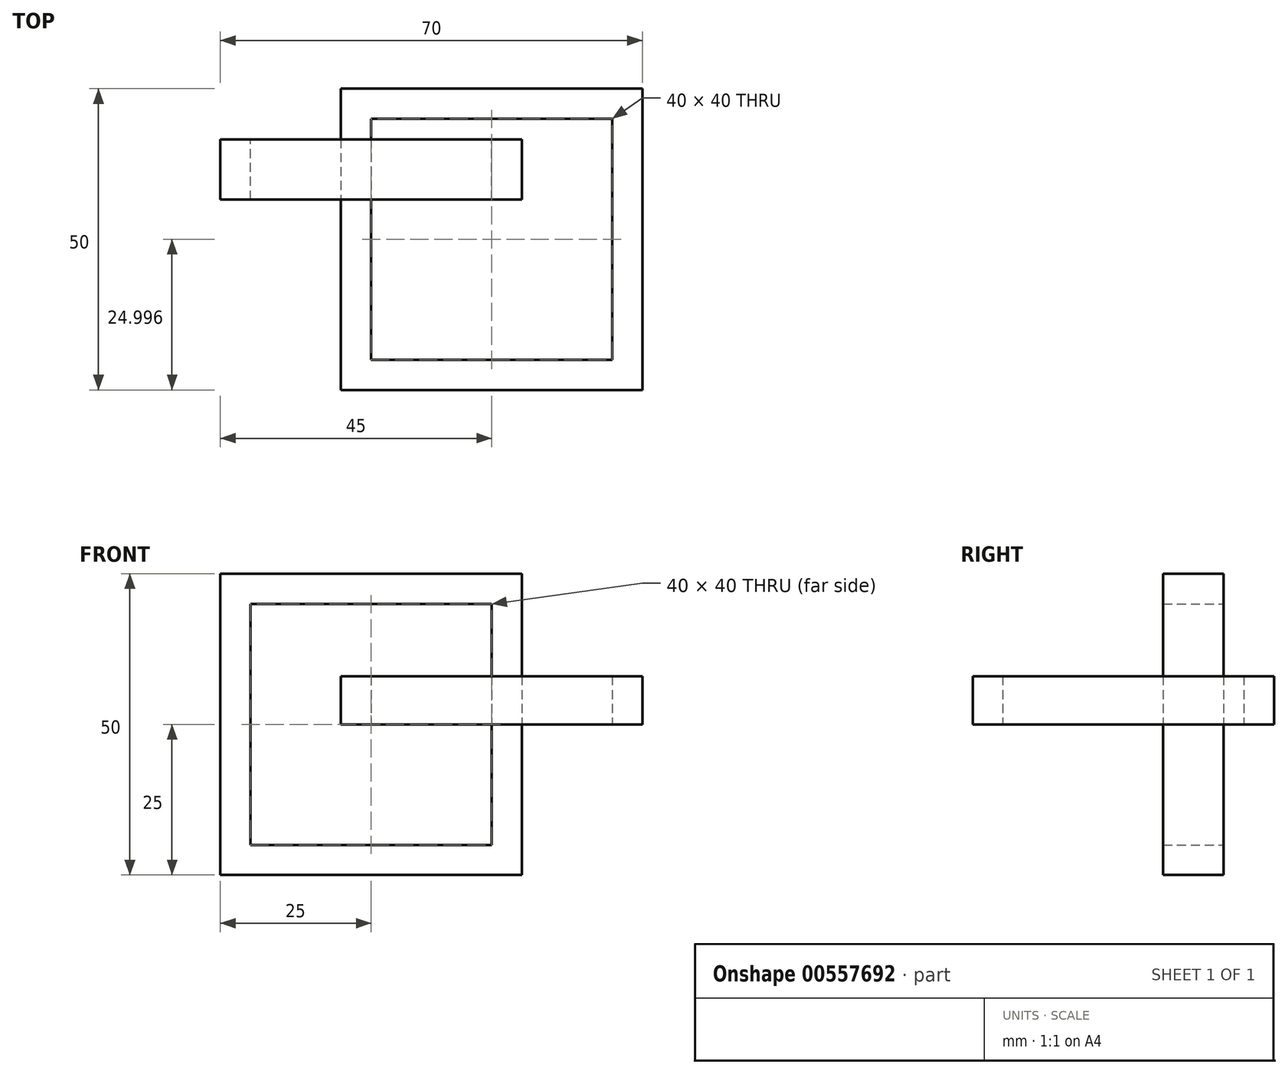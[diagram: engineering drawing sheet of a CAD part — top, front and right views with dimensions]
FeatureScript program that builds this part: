
annotation { "Feature Type Name" : "Feature", "Feature Type Description" : "" }
export const myFeature = defineFeature(function(context is Context, id is Id, definition is map)
    precondition{}
    {
        {
            var Q0;
            Q0=qCreatedBy(makeId("Front.planeOp"),FACE);
            var sketch = newSketch(context, id + "F0", { "sketchPlane" : qUnion([Q0])});
            skLineSegment(sketch, "E0.bottom", {"start": v(-25, 25) * mm, "end": v(25, 25) * mm});
            skLineSegment(sketch, "E0.top", {"start": v(-25, -25) * mm, "end": v(25, -25) * mm});
            skLineSegment(sketch, "E0.left", {"start": v(-25, 25) * mm, "end": v(-25, -25) * mm});
            skLineSegment(sketch, "E0.right", {"start": v(25, 25) * mm, "end": v(25, -25) * mm});
            skPoint(sketch, "E0.middle", {"position": v(0, 0) * mm});
            skLineSegment(sketch, "E1.bottom", {"start": v(-20, 20) * mm, "end": v(20, 20) * mm});
            skLineSegment(sketch, "E1.top", {"start": v(-20, -20) * mm, "end": v(20, -20) * mm});
            skLineSegment(sketch, "E1.left", {"start": v(-20, 20) * mm, "end": v(-20, -20) * mm});
            skLineSegment(sketch, "E1.right", {"start": v(20, 20) * mm, "end": v(20, -20) * mm});
            skSolve(sketch);
        }
        {
            var Q0;
            Q0 = qSketchRegion(id + "F0", true);
            extrude(context, id + "F1", {"entities" : qUnion([Q0]), "depth" : 10 * mm, "offsetDistance" : 25 * mm});
        }
        {
            var Q0;
            Q0=qCreatedBy(makeId("Top.planeOp"),FACE);
            var sketch = newSketch(context, id + "F2", { "sketchPlane" : qUnion([Q0])});
            skLineSegment(sketch, "E2.bottom", {"start": v(-5, 8.4) * mm, "end": v(45, 8.4) * mm});
            skLineSegment(sketch, "E2.top", {"start": v(-5, -41.6) * mm, "end": v(45, -41.6) * mm});
            skLineSegment(sketch, "E2.left", {"start": v(-5, 8.4) * mm, "end": v(-5, -41.6) * mm});
            skLineSegment(sketch, "E2.right", {"start": v(45, 8.4) * mm, "end": v(45, -41.6) * mm});
            skPoint(sketch, "E2.middle", {"position": v(20, -16.6) * mm});
            skLineSegment(sketch, "E3.bottom", {"start": v(0, 3.4) * mm, "end": v(40, 3.4) * mm});
            skLineSegment(sketch, "E3.top", {"start": v(0, -36.6) * mm, "end": v(40, -36.6) * mm});
            skLineSegment(sketch, "E3.left", {"start": v(0, 3.4) * mm, "end": v(0, -36.6) * mm});
            skLineSegment(sketch, "E3.right", {"start": v(40, 3.4) * mm, "end": v(40, -36.6) * mm});
            skSolve(sketch);
        }
        {
            var Q0;
            Q0=makeQuery(id+"F2.imprint","IMPRINT",FACE,{"disambiguationData":[TD([[makeQuery(id+"F2.imprint","IMPRINT",EDGE,{"derivedFrom":sQuery(id+"F2.wireOp",EDGE,"E2.bottom")}),-1.0]])]});
            extrude(context, id + "F3", {"entities" : qUnion([Q0]), "depth" : 8 * mm, "offsetDistance" : 25 * mm});
        }
    });
